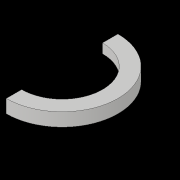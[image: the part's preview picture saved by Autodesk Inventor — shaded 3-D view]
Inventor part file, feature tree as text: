
AUTODESK INVENTOR PART (.ipt)
format: ipt  version: 2017 (Build 210142000, 142)  size: 114,688 bytes
history: native  units: in
note: dims shown in document units (in); Inventor stores cm internally (conversion verified against a paired STEP export)
features: revolve x1, sketch x1
ambient origin geometry x8: Origin, YZ Plane, XZ Plane, XY Plane, X Axis, Y Axis, Z Axis, Center Point
bodies: Solid1 (feature_tree)
feature tree (2):
  revolve  "Revolution1"  [1 undecoded]
  sketch  "Sketch1"  dims[d0=2.0in d2=10.5in d3=2.0in d4=2.875in d5=0.125in d6=0.125in d7=0.125in d8=0.125in d9=0.125in d10=0.125in d11=0.125in d12=0.125in d13=1.0285in d14=0.5in d15=180.0deg d16=5.25in d17=0.125in d18=0.125in d19=0.25in d20=0.0625in d21=0.25in d22=0.25in]
note: 1 required parameter value undecoded (feature->parameter linkage not recoverable at this tier; creation-order binding heuristic only, values carry confidence <= 0.55)
